# Revit family: Lollygagger Go Lounge
name_source: partatom
category: Furniture
revit_build: Autodesk Revit 2016 (Build: 20150220_1215(x64)
units: mm (PartAtom-declared; Revit-internal decimal feet)

## family parameters
Always vertical = Yes
Cut with Voids When Loaded = No
OmniClass Number = 23.40.20.00
OmniClass Title = General Furniture and Specialties
Room Calculation Point = No
Shared = No
Work Plane-Based = No

## types (11) — shared parameters
Apron = 1' - 8"
Height Top = 2' - 1"
Length = 2' - 5 1/8"
Manufacturer = Loll
Thick = 0' - 1"
URL = https://lolldesigns.com
Width = 2' - 5 1/32"

## per-type parameters (varying)
| type | Type Image |
| Loll-Black | go_lounge.jpg |
| Loll-Sunset | go_lounge.jpg |
| Loll-Chocolate | <None> |
| Loll-Sky | go_lounge.jpg |
| Loll-Apple | go_lounge.jpg |
| Loll-Leaf | go_lounge.jpg |
| Loll-Evergreen | go_lounge.jpg |
| Loll-Charcoal | go_lounge.jpg |
| Loll-Sand | go_lounge.jpg |
| Loll-Navy Blue | go_lounge.jpg |
| Loll-White | go_lounge.jpg |

note: column(s) folded — value = type name in every type: Finish Material

## geometry (parser evidence)
native form markers: Sweep x2
no freeform markers — native parametric forms only
